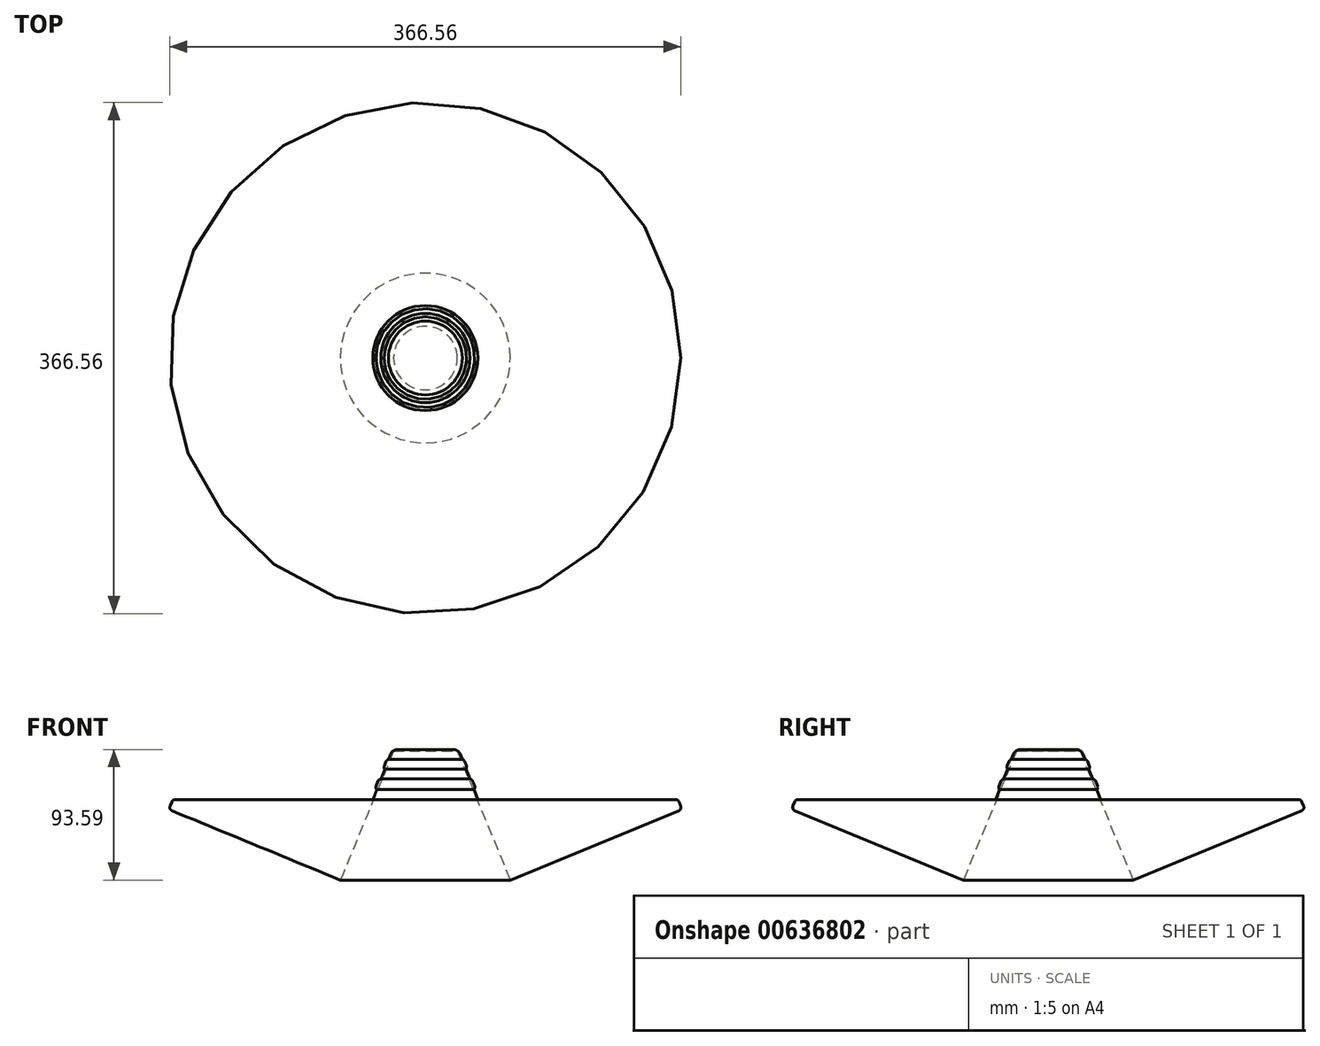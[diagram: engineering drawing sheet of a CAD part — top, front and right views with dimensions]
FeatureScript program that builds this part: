
annotation { "Feature Type Name" : "Feature", "Feature Type Description" : "" }
export const myFeature = defineFeature(function(context is Context, id is Id, definition is map)
    precondition{}
    {
        {
            var Q0;
            Q0=qCreatedBy(makeId("Front.planeOp"),FACE);
            var sketch = newSketch(context, id + "F0", { "sketchPlane" : qUnion([Q0])});
            skLineSegment(sketch, "E0", {"start": v(0, 48.85) * mm, "end": v(23.58, 48.85) * mm});
            skLineSegment(sketch, "E1", {"start": v(23.58, 48.85) * mm, "end": v(26.49, 41.8) * mm});
            skLineSegment(sketch, "E2", {"start": v(26.49, 41.8) * mm, "end": v(27.58, 41.8) * mm});
            skLineSegment(sketch, "E3", {"start": v(27.58, 41.8) * mm, "end": v(30.48, 34.76) * mm});
            skLineSegment(sketch, "E4", {"start": v(30.48, 34.76) * mm, "end": v(29.05, 34.76) * mm});
            skLineSegment(sketch, "E5", {"start": v(29.05, 34.76) * mm, "end": v(31.95, 27.71) * mm});
            skLineSegment(sketch, "E6", {"start": v(31.95, 27.71) * mm, "end": v(33.3, 27.71) * mm});
            skLineSegment(sketch, "E7", {"start": v(33.3, 27.71) * mm, "end": v(36.2, 20.67) * mm});
            skLineSegment(sketch, "E8", {"start": v(36.2, 20.67) * mm, "end": v(34.75, 20.07) * mm});
            skLineSegment(sketch, "E9", {"start": v(34.75, 20.07) * mm, "end": v(37.65, 13.02) * mm});
            skLineSegment(sketch, "E10", {"start": v(37.65, 13.02) * mm, "end": v(181.15, 13.02) * mm});
            skLineSegment(sketch, "E11", {"start": v(181.15, 13.02) * mm, "end": v(184.05, 5.98) * mm});
            skLineSegment(sketch, "E12", {"start": v(184.05, 5.98) * mm, "end": v(60.88, -44.74) * mm});
            skLineSegment(sketch, "E13", {"start": v(60.88, -44.74) * mm, "end": v(22.8, 47.73) * mm});
            skLineSegment(sketch, "E14", {"start": v(22.8, 47.73) * mm, "end": v(0, 47.73) * mm});
            skLineSegment(sketch, "E15", {"start": v(0, 47.73) * mm, "end": v(0, 48.85) * mm});
            skSolve(sketch);
        }
        {
            var Q0;
            Q0 = qSketchRegion(id + "F0", true);
            var Q1;
            Q1=sQuery(id+"F0.wireOp",EDGE,"E15");
            revolve(context, id + "F1", {"entities" : qUnion([Q0]), "axis" : qUnion([Q1]), "revolveType" : RevolveType.FULL});
        }
        {
            var Q0;
            Q0=makeQuery(id+"F1.opRevolve","SWEPT_EDGE",EDGE,{"disambiguationData":[OSD([sQuery(id+"F0.wireOp",EDGE,"E0"),sQuery(id+"F0.wireOp",EDGE,"E1")])]});
            fillet(context, id + "F2", {"entities" : qUnion([Q0]), "radius" : 5.08 * mm, "tangentPropagation" : true, "allowEdgeOverflow" : false});
        }
        {
            var Q0;
            Q0=makeQuery(id+"F1.opRevolve","SWEPT_EDGE",EDGE,{"disambiguationData":[OSD([sQuery(id+"F0.wireOp",EDGE,"E2"),sQuery(id+"F0.wireOp",EDGE,"E3")])]});
            var Q1;
            Q1=makeQuery(id+"F1.opRevolve","SWEPT_EDGE",EDGE,{"disambiguationData":[OSD([sQuery(id+"F0.wireOp",EDGE,"E3"),sQuery(id+"F0.wireOp",EDGE,"E4")])]});
            var Q2;
            Q2=makeQuery(id+"F1.opRevolve","SWEPT_EDGE",EDGE,{"disambiguationData":[OSD([sQuery(id+"F0.wireOp",EDGE,"E6"),sQuery(id+"F0.wireOp",EDGE,"E7")])]});
            var Q3;
            Q3=makeQuery(id+"F1.opRevolve","SWEPT_EDGE",EDGE,{"disambiguationData":[OSD([sQuery(id+"F0.wireOp",EDGE,"E7"),sQuery(id+"F0.wireOp",EDGE,"E8")])]});
            var Q4;
            Q4=makeQuery(id+"F1.opRevolve","SWEPT_EDGE",EDGE,{"disambiguationData":[OSD([sQuery(id+"F0.wireOp",EDGE,"E10"),sQuery(id+"F0.wireOp",EDGE,"E11")])]});
            var Q5;
            Q5=makeQuery(id+"F1.opRevolve","SWEPT_EDGE",EDGE,{"disambiguationData":[OSD([sQuery(id+"F0.wireOp",EDGE,"E11"),sQuery(id+"F0.wireOp",EDGE,"E12")])]});
            fillet(context, id + "F3", {"entities" : qUnion([Q0, Q1, Q2, Q3, Q4, Q5]), "radius" : 2.54 * mm, "tangentPropagation" : true, "allowEdgeOverflow" : false});
        }
    });
